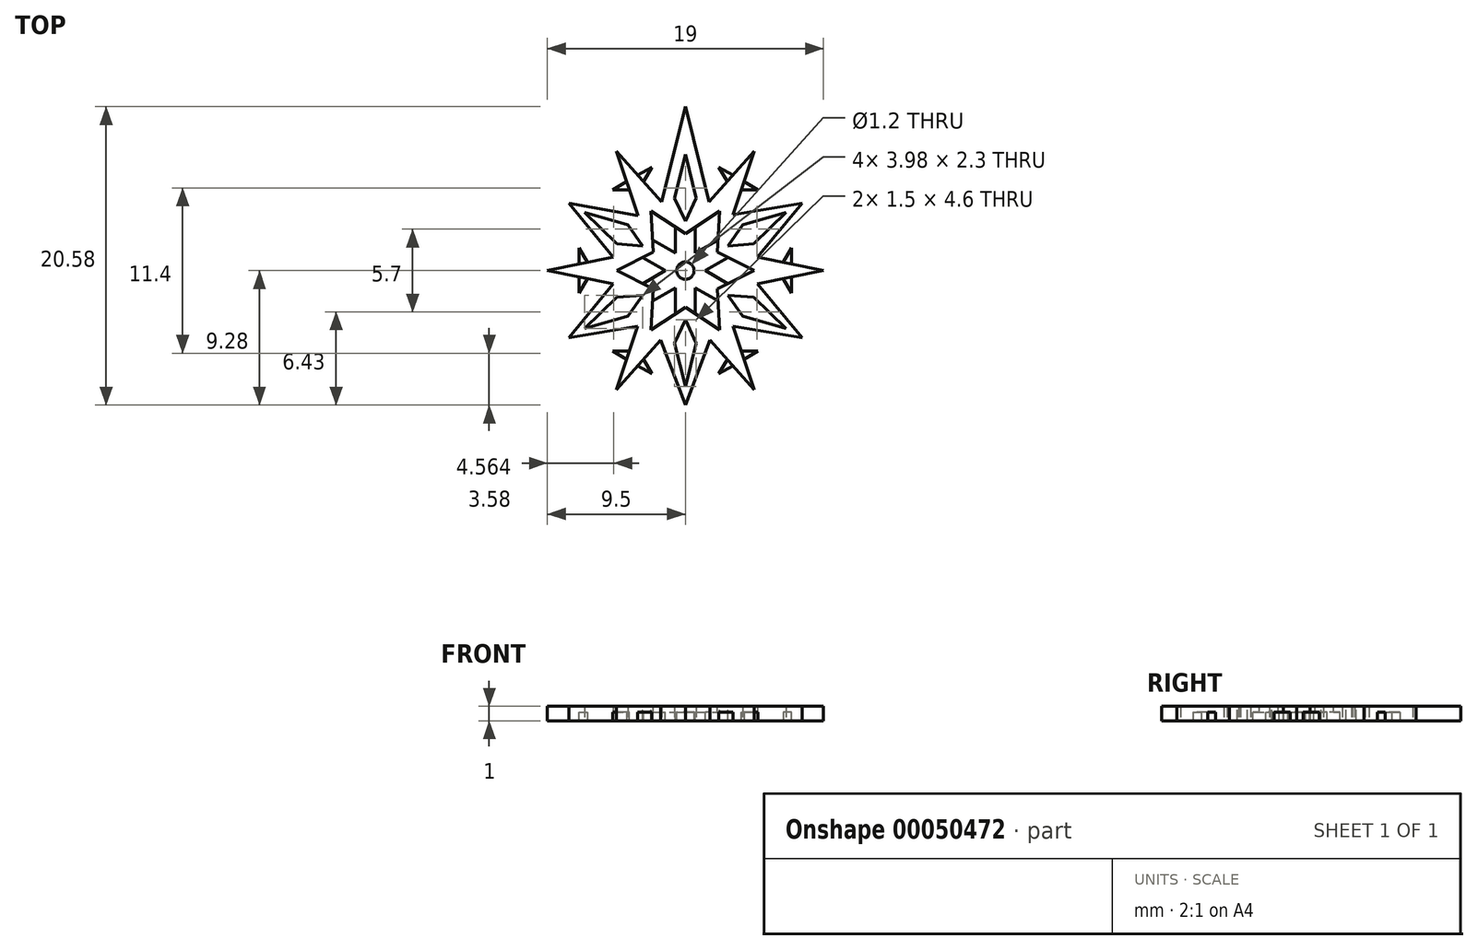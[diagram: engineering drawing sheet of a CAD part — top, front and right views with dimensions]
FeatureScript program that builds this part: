
annotation { "Feature Type Name" : "Feature", "Feature Type Description" : "" }
export const myFeature = defineFeature(function(context is Context, id is Id, definition is map)
    precondition{}
    {
        {
            var Q0;
            Q0=qCreatedBy(makeId("Top.planeOp"),FACE);
            var sketch = newSketch(context, id + "F0", { "sketchPlane" : qUnion([Q0])});
            skArc(sketch, "E0", {"start": v(-1.64, 4.72) * mm, "mid": v(-2.5, 4.33) * mm, "end": v(-3.27, 3.78) * mm});
            skLineSegment(sketch, "E1", {"start": v(-1.64, 4.72) * mm, "end": v(0, 11.3) * mm});
            skLineSegment(sketch, "E2", {"start": v(0, 11.3) * mm, "end": v(1.64, 4.72) * mm});
            skPoint(sketch, "E3.orphan", {"position": v(0, 11.3) * mm});
            skLineSegment(sketch, "E4.1.0", {"start": v(-4.93, 0.86) * mm, "end": v(-8.04, 4.64) * mm});
            skLineSegment(sketch, "E4.1.3", {"start": v(-8.04, 4.64) * mm, "end": v(-3.27, 3.78) * mm});
            skLineSegment(sketch, "E4.2.0", {"start": v(-3.2, -3.84) * mm, "end": v(-8.04, -4.64) * mm});
            skLineSegment(sketch, "E4.2.3", {"start": v(-8.04, -4.64) * mm, "end": v(-4.93, -0.86) * mm});
            skLineSegment(sketch, "E4.3.0", {"start": v(1.72, -4.7) * mm, "end": v(0, -9.28) * mm});
            skLineSegment(sketch, "E4.3.3", {"start": v(0, -9.28) * mm, "end": v(-1.72, -4.7) * mm});
            skLineSegment(sketch, "E4.4.0", {"start": v(4.93, -0.86) * mm, "end": v(8.04, -4.64) * mm});
            skLineSegment(sketch, "E4.4.3", {"start": v(8.04, -4.64) * mm, "end": v(3.2, -3.84) * mm});
            skLineSegment(sketch, "E4.5.0", {"start": v(3.2, 3.84) * mm, "end": v(8.04, 4.64) * mm});
            skLineSegment(sketch, "E4.5.3", {"start": v(8.04, 4.64) * mm, "end": v(4.93, 0.86) * mm});
            skArc(sketch, "E5.trimOffspring", {"start": v(3.2, 3.84) * mm, "mid": v(2.47, 4.35) * mm, "end": v(1.64, 4.72) * mm});
            skArc(sketch, "E6.trimOffspring", {"start": v(-4.93, 0.86) * mm, "mid": v(-5, 0) * mm, "end": v(-4.93, -0.86) * mm});
            skArc(sketch, "E7.trimOffspring", {"start": v(4.93, -0.86) * mm, "mid": v(5, 0) * mm, "end": v(4.93, 0.86) * mm});
            skArc(sketch, "E8.trimOffspring", {"start": v(1.72, -4.7) * mm, "mid": v(2.5, -4.33) * mm, "end": v(3.2, -3.84) * mm});
            skArc(sketch, "E9.trimOffspring", {"start": v(-3.2, -3.84) * mm, "mid": v(-2.5, -4.33) * mm, "end": v(-1.72, -4.7) * mm});
            skLineSegment(sketch, "E10", {"start": v(0, 8) * mm, "end": v(0.75, 5) * mm});
            skLineSegment(sketch, "E11", {"start": v(0.75, 5) * mm, "end": v(-0.75, 5) * mm});
            skLineSegment(sketch, "E12", {"start": v(-0.75, 5) * mm, "end": v(0, 8) * mm});
            skLineSegment(sketch, "E13.1.0", {"start": v(-4.7, 1.85) * mm, "end": v(-6.93, 4) * mm});
            skLineSegment(sketch, "E13.1.1", {"start": v(-6.93, 4) * mm, "end": v(-3.96, 3.15) * mm});
            skLineSegment(sketch, "E13.1.2", {"start": v(-3.96, 3.15) * mm, "end": v(-4.7, 1.85) * mm});
            skLineSegment(sketch, "E13.2.0", {"start": v(-3.96, -3.15) * mm, "end": v(-6.93, -4) * mm});
            skLineSegment(sketch, "E13.2.1", {"start": v(-6.93, -4) * mm, "end": v(-4.7, -1.85) * mm});
            skLineSegment(sketch, "E13.2.2", {"start": v(-4.7, -1.85) * mm, "end": v(-3.96, -3.15) * mm});
            skLineSegment(sketch, "E13.3.0", {"start": v(0.75, -5) * mm, "end": v(0, -8) * mm});
            skLineSegment(sketch, "E13.3.1", {"start": v(0, -8) * mm, "end": v(-0.75, -5) * mm});
            skLineSegment(sketch, "E13.3.2", {"start": v(-0.75, -5) * mm, "end": v(0.75, -5) * mm});
            skLineSegment(sketch, "E13.4.0", {"start": v(4.7, -1.85) * mm, "end": v(6.93, -4) * mm});
            skLineSegment(sketch, "E13.4.1", {"start": v(6.93, -4) * mm, "end": v(3.96, -3.15) * mm});
            skLineSegment(sketch, "E13.4.2", {"start": v(3.96, -3.15) * mm, "end": v(4.7, -1.85) * mm});
            skLineSegment(sketch, "E13.5.0", {"start": v(3.96, 3.15) * mm, "end": v(6.93, 4) * mm});
            skLineSegment(sketch, "E13.5.1", {"start": v(6.93, 4) * mm, "end": v(4.7, 1.85) * mm});
            skLineSegment(sketch, "E13.5.2", {"start": v(4.7, 1.85) * mm, "end": v(3.96, 3.15) * mm});
            skLineSegment(sketch, "E14", {"start": v(-3.27, 3.78) * mm, "end": v(-4.75, 8.23) * mm});
            skLineSegment(sketch, "E15", {"start": v(-4.75, 8.23) * mm, "end": v(-1.64, 4.72) * mm});
            skLineSegment(sketch, "E16", {"start": v(-4.75, 8.23) * mm, "end": v(-2.5, 4.33) * mm, "construction": true});
            skLineSegment(sketch, "E17.1.0", {"start": v(-9.5, 0) * mm, "end": v(-4.91, 0.94) * mm});
            skLineSegment(sketch, "E17.1.1", {"start": v(-4.91, -0.94) * mm, "end": v(-9.5, 0) * mm});
            skLineSegment(sketch, "E17.2.0", {"start": v(-4.75, -8.23) * mm, "end": v(-3.27, -3.78) * mm});
            skLineSegment(sketch, "E17.2.1", {"start": v(-1.64, -4.72) * mm, "end": v(-4.75, -8.23) * mm});
            skLineSegment(sketch, "E17.3.0", {"start": v(4.75, -8.23) * mm, "end": v(1.64, -4.72) * mm});
            skLineSegment(sketch, "E17.3.1", {"start": v(3.27, -3.78) * mm, "end": v(4.75, -8.23) * mm});
            skLineSegment(sketch, "E17.4.0", {"start": v(9.5, 0) * mm, "end": v(4.91, -0.94) * mm});
            skLineSegment(sketch, "E17.4.1", {"start": v(4.91, 0.94) * mm, "end": v(9.5, 0) * mm});
            skLineSegment(sketch, "E17.5.0", {"start": v(4.75, 8.23) * mm, "end": v(3.27, 3.78) * mm});
            skLineSegment(sketch, "E17.5.1", {"start": v(1.64, 4.72) * mm, "end": v(4.75, 8.23) * mm});
            skSolve(sketch);
        }
        {
            var Q0;
            Q0=qSketchRegion(id+"F0",true);
            extrude(context, id + "F1", {"entities" : qUnion([Q0]), "depth" : 1 * mm});
        }
        {
            var Q0;
            Q0=makeQuery(id+"F1.opExtrude","CAP_FACE",FACE,{"disambiguationData":[OSD([sQuery(id+"F0.wireOp",EDGE,"E0"),sQuery(id+"F0.wireOp",EDGE,"E1"),sQuery(id+"F0.wireOp",EDGE,"E2"),sQuery(id+"F0.wireOp",EDGE,"1b853f63-bc8d-4a45-9e58-fd6dd771b944"),sQuery(id+"F0.wireOp",EDGE,"199b02c5-8d33-4c38-8ebd-d630f5a1a6e4"),sQuery(id+"F0.wireOp",EDGE,"8d3cd1ca-bb38-4595-ae14-e456ec82a749.filletArc"),sQuery(id+"F0.wireOp",EDGE,"E4.1.0"),sQuery(id+"F0.wireOp",EDGE,"E4.1.1"),sQuery(id+"F0.wireOp",EDGE,"E4.1.2"),sQuery(id+"F0.wireOp",EDGE,"E4.1.3"),sQuery(id+"F0.wireOp",EDGE,"E4.1.4"),sQuery(id+"F0.wireOp",EDGE,"E4.2.0"),sQuery(id+"F0.wireOp",EDGE,"E4.2.1"),sQuery(id+"F0.wireOp",EDGE,"E4.2.2"),sQuery(id+"F0.wireOp",EDGE,"E4.2.3"),sQuery(id+"F0.wireOp",EDGE,"E4.2.4"),sQuery(id+"F0.wireOp",EDGE,"E4.3.0"),sQuery(id+"F0.wireOp",EDGE,"E4.3.1"),sQuery(id+"F0.wireOp",EDGE,"E4.3.2"),sQuery(id+"F0.wireOp",EDGE,"E4.3.3"),sQuery(id+"F0.wireOp",EDGE,"E4.3.4"),sQuery(id+"F0.wireOp",EDGE,"E4.4.0"),sQuery(id+"F0.wireOp",EDGE,"E4.4.1"),sQuery(id+"F0.wireOp",EDGE,"E4.4.2"),sQuery(id+"F0.wireOp",EDGE,"E4.4.3"),sQuery(id+"F0.wireOp",EDGE,"E4.4.4"),sQuery(id+"F0.wireOp",EDGE,"E4.5.0"),sQuery(id+"F0.wireOp",EDGE,"E4.5.1"),sQuery(id+"F0.wireOp",EDGE,"E4.5.2"),sQuery(id+"F0.wireOp",EDGE,"E4.5.3"),sQuery(id+"F0.wireOp",EDGE,"E4.5.4"),sQuery(id+"F0.wireOp",EDGE,"E5.trimOffspring"),sQuery(id+"F0.wireOp",EDGE,"E6.trimOffspring"),sQuery(id+"F0.wireOp",EDGE,"E7.trimOffspring"),sQuery(id+"F0.wireOp",EDGE,"E8.trimOffspring"),sQuery(id+"F0.wireOp",EDGE,"E9.trimOffspring"),sQuery(id+"F0.wireOp",EDGE,"E10"),sQuery(id+"F0.wireOp",EDGE,"E11"),sQuery(id+"F0.wireOp",EDGE,"E12"),sQuery(id+"F0.wireOp",EDGE,"E13.1.0"),sQuery(id+"F0.wireOp",EDGE,"E13.1.1"),sQuery(id+"F0.wireOp",EDGE,"E13.1.2"),sQuery(id+"F0.wireOp",EDGE,"E13.2.0"),sQuery(id+"F0.wireOp",EDGE,"E13.2.1"),sQuery(id+"F0.wireOp",EDGE,"E13.2.2"),sQuery(id+"F0.wireOp",EDGE,"E13.3.0"),sQuery(id+"F0.wireOp",EDGE,"E13.3.1"),sQuery(id+"F0.wireOp",EDGE,"E13.3.2"),sQuery(id+"F0.wireOp",EDGE,"E13.4.0"),sQuery(id+"F0.wireOp",EDGE,"E13.4.1"),sQuery(id+"F0.wireOp",EDGE,"E13.4.2"),sQuery(id+"F0.wireOp",EDGE,"E13.5.0"),sQuery(id+"F0.wireOp",EDGE,"E13.5.1"),sQuery(id+"F0.wireOp",EDGE,"E13.5.2")])],"isStart":false});
            var sketch = newSketch(context, id + "F2", { "sketchPlane" : qUnion([Q0])});
            skLineSegment(sketch, "E18", {"start": v(-0.75, 5) * mm, "end": v(0.75, 5) * mm});
            skLineSegment(sketch, "E19", {"start": v(0.75, 5) * mm, "end": v(0, 3.4) * mm});
            skLineSegment(sketch, "E20", {"start": v(0, 3.4) * mm, "end": v(-0.75, 5) * mm});
            skLineSegment(sketch, "E21", {"start": v(0.7, 3) * mm, "end": v(0.7, 1.2) * mm});
            skLineSegment(sketch, "E22", {"start": v(0.7, 1.2) * mm, "end": v(2.25, 2.1) * mm});
            skLineSegment(sketch, "E23", {"start": v(2.25, 2.1) * mm, "end": v(2.37, 4.1) * mm});
            skLineSegment(sketch, "E24", {"start": v(2.37, 4.1) * mm, "end": v(0.7, 3) * mm});
            skLineSegment(sketch, "E25", {"start": v(0, 0) * mm, "end": v(2.37, 4.1) * mm, "construction": true});
            skLineSegment(sketch, "E26", {"start": v(2.95, 0) * mm, "end": v(0, 0) * mm, "construction": true});
            skLineSegment(sketch, "E27", {"start": v(0, 3.4) * mm, "end": v(0.7, 3) * mm, "construction": true});
            skLineSegment(sketch, "E28.1.0", {"start": v(-3.96, 3.15) * mm, "end": v(-2.94, 1.7) * mm});
            skLineSegment(sketch, "E28.1.1", {"start": v(-2.94, 1.7) * mm, "end": v(-4.7, 1.85) * mm});
            skLineSegment(sketch, "E28.1.2", {"start": v(-4.7, 1.85) * mm, "end": v(-3.96, 3.15) * mm});
            skLineSegment(sketch, "E28.1.3", {"start": v(-2.37, 4.1) * mm, "end": v(-2.25, 2.1) * mm});
            skLineSegment(sketch, "E28.1.4", {"start": v(-2.25, 2.1) * mm, "end": v(-0.7, 1.2) * mm});
            skLineSegment(sketch, "E28.1.5", {"start": v(-0.7, 1.2) * mm, "end": v(-0.7, 3) * mm});
            skLineSegment(sketch, "E28.1.6", {"start": v(-0.7, 3) * mm, "end": v(-2.37, 4.1) * mm});
            skLineSegment(sketch, "E28.2.0", {"start": v(-4.7, -1.85) * mm, "end": v(-2.94, -1.7) * mm});
            skLineSegment(sketch, "E28.2.1", {"start": v(-2.94, -1.7) * mm, "end": v(-3.96, -3.15) * mm});
            skLineSegment(sketch, "E28.2.2", {"start": v(-3.96, -3.15) * mm, "end": v(-4.7, -1.85) * mm});
            skLineSegment(sketch, "E28.2.3", {"start": v(-4.73, 0) * mm, "end": v(-2.94, -0.9) * mm});
            skLineSegment(sketch, "E28.2.4", {"start": v(-2.94, -0.9) * mm, "end": v(-1.39, 0) * mm});
            skLineSegment(sketch, "E28.2.5", {"start": v(-1.39, 0) * mm, "end": v(-2.94, 0.9) * mm});
            skLineSegment(sketch, "E28.2.6", {"start": v(-2.94, 0.9) * mm, "end": v(-4.73, 0) * mm});
            skLineSegment(sketch, "E28.3.0", {"start": v(-0.75, -5) * mm, "end": v(0, -3.4) * mm});
            skLineSegment(sketch, "E28.3.1", {"start": v(0, -3.4) * mm, "end": v(0.75, -5) * mm});
            skLineSegment(sketch, "E28.3.2", {"start": v(0.75, -5) * mm, "end": v(-0.75, -5) * mm});
            skLineSegment(sketch, "E28.3.3", {"start": v(-2.37, -4.1) * mm, "end": v(-0.7, -3) * mm});
            skLineSegment(sketch, "E28.3.4", {"start": v(-0.7, -3) * mm, "end": v(-0.7, -1.2) * mm});
            skLineSegment(sketch, "E28.3.5", {"start": v(-0.7, -1.2) * mm, "end": v(-2.25, -2.1) * mm});
            skLineSegment(sketch, "E28.3.6", {"start": v(-2.25, -2.1) * mm, "end": v(-2.37, -4.1) * mm});
            skLineSegment(sketch, "E28.4.0", {"start": v(3.96, -3.15) * mm, "end": v(2.94, -1.7) * mm});
            skLineSegment(sketch, "E28.4.1", {"start": v(2.94, -1.7) * mm, "end": v(4.7, -1.85) * mm});
            skLineSegment(sketch, "E28.4.2", {"start": v(4.7, -1.85) * mm, "end": v(3.96, -3.15) * mm});
            skLineSegment(sketch, "E28.4.3", {"start": v(2.37, -4.1) * mm, "end": v(2.25, -2.1) * mm});
            skLineSegment(sketch, "E28.4.4", {"start": v(2.25, -2.1) * mm, "end": v(0.7, -1.2) * mm});
            skLineSegment(sketch, "E28.4.5", {"start": v(0.7, -1.2) * mm, "end": v(0.7, -3) * mm});
            skLineSegment(sketch, "E28.4.6", {"start": v(0.7, -3) * mm, "end": v(2.37, -4.1) * mm});
            skLineSegment(sketch, "E28.5.0", {"start": v(4.7, 1.85) * mm, "end": v(2.94, 1.7) * mm});
            skLineSegment(sketch, "E28.5.1", {"start": v(2.94, 1.7) * mm, "end": v(3.96, 3.15) * mm});
            skLineSegment(sketch, "E28.5.2", {"start": v(3.96, 3.15) * mm, "end": v(4.7, 1.85) * mm});
            skLineSegment(sketch, "E28.5.3", {"start": v(4.73, 0) * mm, "end": v(2.94, 0.9) * mm});
            skLineSegment(sketch, "E28.5.4", {"start": v(2.94, 0.9) * mm, "end": v(1.39, 0) * mm});
            skLineSegment(sketch, "E28.5.5", {"start": v(1.39, 0) * mm, "end": v(2.94, -0.9) * mm});
            skLineSegment(sketch, "E28.5.6", {"start": v(2.94, -0.9) * mm, "end": v(4.73, 0) * mm});
            skPoint(sketch, "E28.center", {"position": v(0, 0) * mm});
            skCircle(sketch, "E29", {"center": v(0, 0) * mm, "radius": 0.6 * mm});
            skSolve(sketch);
        }
        {
            var Q0;
            Q0=qSketchRegion(id+"F2",true);
            extrude(context, id + "F3", {"entities" : qUnion([Q0]), "operationType" : NewBodyOperationType.REMOVE, "oppositeDirection" : true, "depth" : 25 * mm});
        }
        {
            var Q0;
            Q0=makeQuery(id+"F1.opExtrude","CAP_FACE",FACE,{"disambiguationData":[OSD([sQuery(id+"F0.wireOp",EDGE,"E1"),sQuery(id+"F0.wireOp",EDGE,"E2"),sQuery(id+"F0.wireOp",EDGE,"E4.1.0"),sQuery(id+"F0.wireOp",EDGE,"E4.1.3"),sQuery(id+"F0.wireOp",EDGE,"E4.2.0"),sQuery(id+"F0.wireOp",EDGE,"E4.2.3"),sQuery(id+"F0.wireOp",EDGE,"E4.3.0"),sQuery(id+"F0.wireOp",EDGE,"E4.3.3"),sQuery(id+"F0.wireOp",EDGE,"E4.4.0"),sQuery(id+"F0.wireOp",EDGE,"E4.4.3"),sQuery(id+"F0.wireOp",EDGE,"E4.5.0"),sQuery(id+"F0.wireOp",EDGE,"E4.5.3"),sQuery(id+"F0.wireOp",EDGE,"E10"),sQuery(id+"F0.wireOp",EDGE,"E11"),sQuery(id+"F0.wireOp",EDGE,"E12"),sQuery(id+"F0.wireOp",EDGE,"E13.1.0"),sQuery(id+"F0.wireOp",EDGE,"E13.1.1"),sQuery(id+"F0.wireOp",EDGE,"E13.1.2"),sQuery(id+"F0.wireOp",EDGE,"E13.2.0"),sQuery(id+"F0.wireOp",EDGE,"E13.2.1"),sQuery(id+"F0.wireOp",EDGE,"E13.2.2"),sQuery(id+"F0.wireOp",EDGE,"E13.3.0"),sQuery(id+"F0.wireOp",EDGE,"E13.3.1"),sQuery(id+"F0.wireOp",EDGE,"E13.3.2"),sQuery(id+"F0.wireOp",EDGE,"E13.4.0"),sQuery(id+"F0.wireOp",EDGE,"E13.4.1"),sQuery(id+"F0.wireOp",EDGE,"E13.4.2"),sQuery(id+"F0.wireOp",EDGE,"E13.5.0"),sQuery(id+"F0.wireOp",EDGE,"E13.5.1"),sQuery(id+"F0.wireOp",EDGE,"E13.5.2"),sQuery(id+"F0.wireOp",EDGE,"E14"),sQuery(id+"F0.wireOp",EDGE,"E15"),sQuery(id+"F0.wireOp",EDGE,"E17.1.0"),sQuery(id+"F0.wireOp",EDGE,"E17.1.1"),sQuery(id+"F0.wireOp",EDGE,"E17.2.0"),sQuery(id+"F0.wireOp",EDGE,"E17.2.1"),sQuery(id+"F0.wireOp",EDGE,"E17.3.0"),sQuery(id+"F0.wireOp",EDGE,"E17.3.1"),sQuery(id+"F0.wireOp",EDGE,"E17.4.0"),sQuery(id+"F0.wireOp",EDGE,"E17.4.1"),sQuery(id+"F0.wireOp",EDGE,"E17.5.0"),sQuery(id+"F0.wireOp",EDGE,"E17.5.1")])],"isStart":false});
            var sketch = newSketch(context, id + "F4", { "sketchPlane" : qUnion([Q0])});
            skLineSegment(sketch, "E30", {"start": v(-0.7, 3) * mm, "end": v(0, 2.55) * mm});
            skLineSegment(sketch, "E31", {"start": v(0, 2.55) * mm, "end": v(0.7, 3) * mm});
            skLineSegment(sketch, "E32", {"start": v(2.25, 2.1) * mm, "end": v(2.2, 1.27) * mm});
            skLineSegment(sketch, "E33", {"start": v(2.2, 1.27) * mm, "end": v(2.94, 0.9) * mm});
            skLineSegment(sketch, "E34", {"start": v(2.94, -0.9) * mm, "end": v(2.2, -1.27) * mm});
            skLineSegment(sketch, "E35", {"start": v(2.2, -1.27) * mm, "end": v(2.25, -2.1) * mm});
            skLineSegment(sketch, "E36", {"start": v(0.7, -3) * mm, "end": v(0, -2.55) * mm});
            skLineSegment(sketch, "E37", {"start": v(0, -2.55) * mm, "end": v(-0.7, -3) * mm});
            skLineSegment(sketch, "E38", {"start": v(-2.25, -2.1) * mm, "end": v(-2.2, -1.27) * mm});
            skLineSegment(sketch, "E39", {"start": v(-2.2, -1.27) * mm, "end": v(-2.94, -0.9) * mm});
            skLineSegment(sketch, "E40", {"start": v(-2.94, 0.9) * mm, "end": v(-2.2, 1.27) * mm});
            skLineSegment(sketch, "E41", {"start": v(-2.2, 1.27) * mm, "end": v(-2.25, 2.1) * mm});
            skLineSegment(sketch, "E42", {"start": v(-2.25, 2.1) * mm, "end": v(-0.7, 1.2) * mm});
            skLineSegment(sketch, "E43", {"start": v(-0.7, 1.2) * mm, "end": v(-0.7, 3) * mm});
            skLineSegment(sketch, "E44", {"start": v(0.7, 3) * mm, "end": v(0.7, 1.2) * mm});
            skLineSegment(sketch, "E45", {"start": v(0.7, 1.2) * mm, "end": v(2.25, 2.1) * mm});
            skLineSegment(sketch, "E46", {"start": v(2.94, 0.9) * mm, "end": v(1.39, 0) * mm});
            skLineSegment(sketch, "E47", {"start": v(1.39, 0) * mm, "end": v(2.94, -0.9) * mm});
            skLineSegment(sketch, "E48", {"start": v(2.25, -2.1) * mm, "end": v(0.7, -1.2) * mm});
            skLineSegment(sketch, "E49", {"start": v(0.7, -1.2) * mm, "end": v(0.7, -3) * mm});
            skLineSegment(sketch, "E50", {"start": v(-0.7, -3) * mm, "end": v(-0.7, -1.2) * mm});
            skLineSegment(sketch, "E51", {"start": v(-0.7, -1.2) * mm, "end": v(-2.25, -2.1) * mm});
            skLineSegment(sketch, "E52", {"start": v(-2.94, -0.9) * mm, "end": v(-1.39, 0) * mm});
            skLineSegment(sketch, "E53", {"start": v(-1.39, 0) * mm, "end": v(-2.94, 0.9) * mm});
            skSolve(sketch);
        }
        {
            var Q0;
            Q0=qSketchRegion(id+"F4",true);
            extrude(context, id + "F5", {"entities" : qUnion([Q0]), "operationType" : NewBodyOperationType.REMOVE, "oppositeDirection" : true, "depth" : 0.4 * mm});
        }
        {
            var Q0;
            Q0=qCreatedBy(makeId("Top.planeOp"),FACE);
            var sketch = newSketch(context, id + "F6", { "sketchPlane" : qUnion([Q0])});
            skLineSegment(sketch, "E54", {"start": v(-5.01, 5.56) * mm, "end": v(-2.31, 7.12) * mm});
            skLineSegment(sketch, "E55", {"start": v(-2.31, 7.12) * mm, "end": v(-3.21, 5.56) * mm});
            skLineSegment(sketch, "E56", {"start": v(-3.21, 5.56) * mm, "end": v(-5.01, 5.56) * mm});
            skLineSegment(sketch, "E57", {"start": v(-4.75, 8.23) * mm, "end": v(-2.37, 4.1) * mm, "construction": true});
            skLineSegment(sketch, "E58.1.0", {"start": v(-7.32, -1.56) * mm, "end": v(-7.32, 1.56) * mm});
            skLineSegment(sketch, "E58.1.1", {"start": v(-6.42, 0) * mm, "end": v(-7.32, -1.56) * mm});
            skLineSegment(sketch, "E58.1.2", {"start": v(-7.32, 1.56) * mm, "end": v(-6.42, 0) * mm});
            skLineSegment(sketch, "E58.2.0", {"start": v(-2.31, -7.12) * mm, "end": v(-5.01, -5.56) * mm});
            skLineSegment(sketch, "E58.2.1", {"start": v(-3.21, -5.56) * mm, "end": v(-2.31, -7.12) * mm});
            skLineSegment(sketch, "E58.2.2", {"start": v(-5.01, -5.56) * mm, "end": v(-3.21, -5.56) * mm});
            skLineSegment(sketch, "E58.3.0", {"start": v(5.01, -5.56) * mm, "end": v(2.31, -7.12) * mm});
            skLineSegment(sketch, "E58.3.1", {"start": v(3.21, -5.56) * mm, "end": v(5.01, -5.56) * mm});
            skLineSegment(sketch, "E58.3.2", {"start": v(2.31, -7.12) * mm, "end": v(3.21, -5.56) * mm});
            skLineSegment(sketch, "E58.4.0", {"start": v(7.32, 1.56) * mm, "end": v(7.32, -1.56) * mm});
            skLineSegment(sketch, "E58.4.1", {"start": v(6.42, 0) * mm, "end": v(7.32, 1.56) * mm});
            skLineSegment(sketch, "E58.4.2", {"start": v(7.32, -1.56) * mm, "end": v(6.42, 0) * mm});
            skLineSegment(sketch, "E58.5.0", {"start": v(2.31, 7.12) * mm, "end": v(5.01, 5.56) * mm});
            skLineSegment(sketch, "E58.5.1", {"start": v(3.21, 5.56) * mm, "end": v(2.31, 7.12) * mm});
            skLineSegment(sketch, "E58.5.2", {"start": v(5.01, 5.56) * mm, "end": v(3.21, 5.56) * mm});
            skPoint(sketch, "E58.center", {"position": v(0, 0) * mm});
            skSolve(sketch);
        }
        {
            var Q0;
            Q0 = qSketchRegion(id + "F6", true);
            extrude(context, id + "F7", {"entities" : qUnion([Q0]), "operationType" : NewBodyOperationType.ADD, "depth" : .6 * mm});
        }
    });
